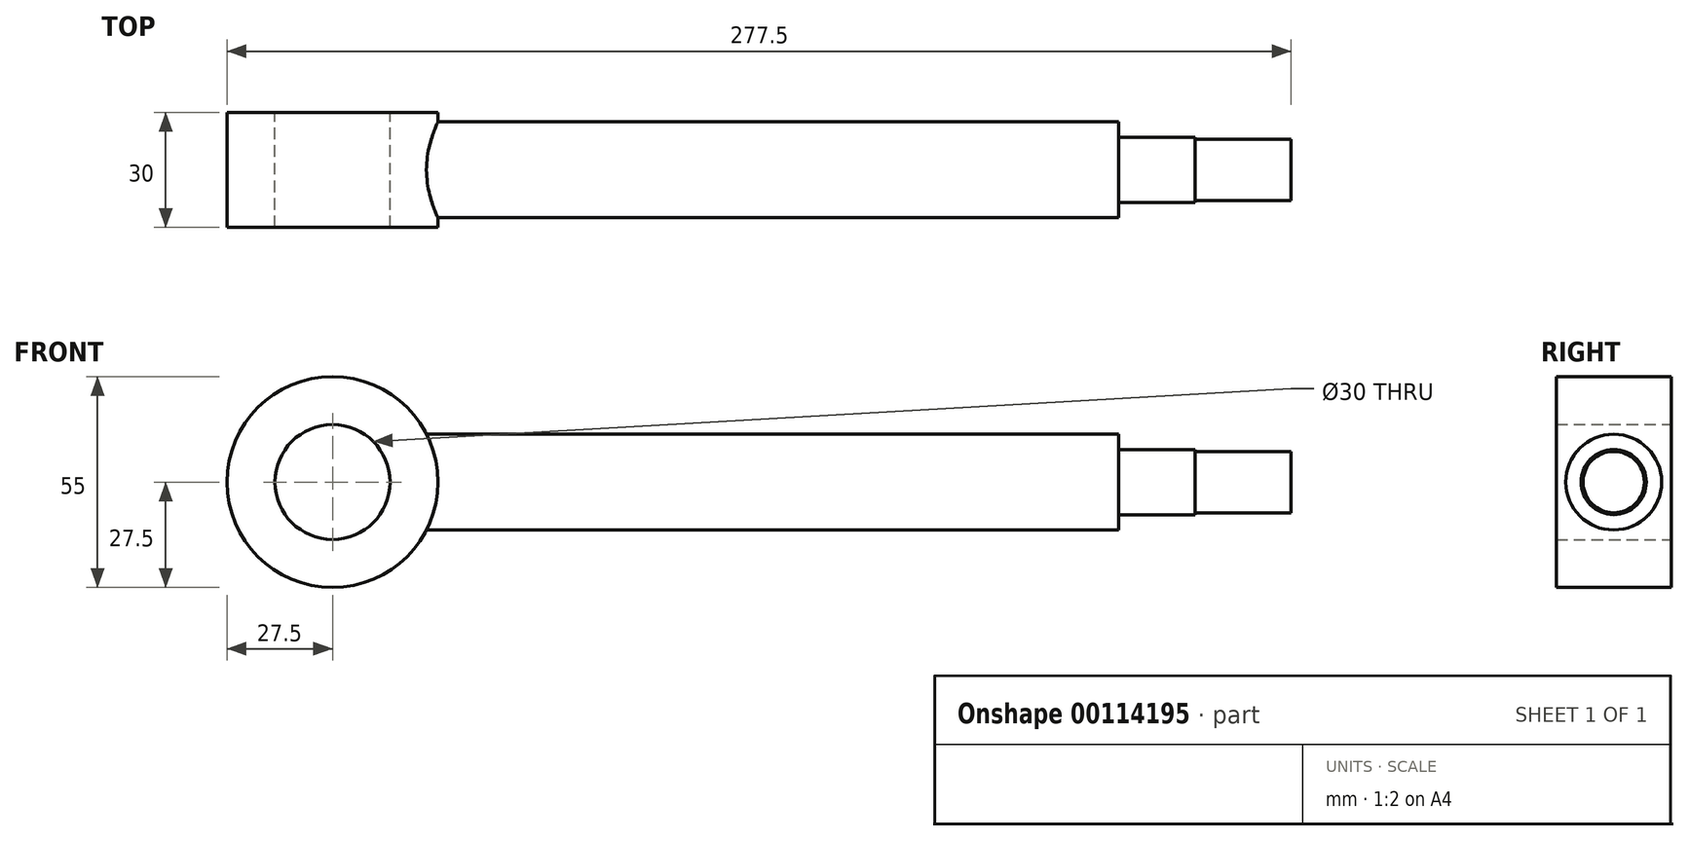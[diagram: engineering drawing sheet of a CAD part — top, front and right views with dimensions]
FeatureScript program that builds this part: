
annotation { "Feature Type Name" : "Feature", "Feature Type Description" : "" }
export const myFeature = defineFeature(function(context is Context, id is Id, definition is map)
    precondition{}
    {
        {
            var Q0;
            Q0=qCreatedBy(makeId("Front.planeOp"),FACE);
            var sketch = newSketch(context, id + "F0", { "sketchPlane" : qUnion([Q0])});
            skLineSegment(sketch, "E0", {"start": v(0, 0) * mm, "end": v(250.98, 0) * mm});
            skCircle(sketch, "E1", {"center": v(0, 0) * mm, "radius": 15 * mm});
            skCircle(sketch, "E2", {"center": v(0, 0) * mm, "radius": 27.5 * mm});
            skLineSegment(sketch, "E3", {"start": v(24.5, 12.5) * mm, "end": v(205, 12.5) * mm});
            skLineSegment(sketch, "E4", {"start": v(250, 8) * mm, "end": v(250, 0) * mm});
            skLineSegment(sketch, "E5", {"start": v(205, 12.5) * mm, "end": v(205, 8.5) * mm});
            skLineSegment(sketch, "E6", {"start": v(205, 8.5) * mm, "end": v(225, 8.5) * mm});
            skLineSegment(sketch, "E7", {"start": v(225, 8.5) * mm, "end": v(225, 8) * mm});
            skLineSegment(sketch, "E8", {"start": v(225, 8) * mm, "end": v(250, 8) * mm});
            skSolve(sketch);
        }
        {
            var Q0;
            Q0=qCreatedBy(makeId("Front.planeOp"),FACE);
            var sketch = newSketch(context, id + "F1", { "sketchPlane" : qUnion([Q0])});
            skLineSegment(sketch, "E9", {"start": v(54.7, 12.5) * mm, "end": v(54.7, 29) * mm});
            skLineSegment(sketch, "E10", {"start": v(54.7, 29) * mm, "end": v(60.7, 29) * mm});
            skLineSegment(sketch, "E11", {"start": v(60.7, 29) * mm, "end": v(60.7, 27.5) * mm});
            skLineSegment(sketch, "E12", {"start": v(60.7, 27.5) * mm, "end": v(76.24, 27.5) * mm});
            skLineSegment(sketch, "E13", {"start": v(76.24, 27.5) * mm, "end": v(79.7, 25.5) * mm});
            skLineSegment(sketch, "E14", {"start": v(79.7, 25.5) * mm, "end": v(94.7, 25.5) * mm});
            skLineSegment(sketch, "E15", {"start": v(94.7, 25.5) * mm, "end": v(94.7, 12.5) * mm});
            skLineSegment(sketch, "E16", {"start": v(94.7, 12.5) * mm, "end": v(54.7, 12.5) * mm});
            skLineSegment(sketch, "E17", {"start": v(66.7, 12.5) * mm, "end": v(66.7, 18) * mm});
            skLineSegment(sketch, "E18", {"start": v(66.7, 18) * mm, "end": v(76.7, 18) * mm});
            skLineSegment(sketch, "E19", {"start": v(76.7, 18) * mm, "end": v(76.7, 12.5) * mm});
            skLineSegment(sketch, "E20", {"start": v(54.7, 14) * mm, "end": v(56.7, 14) * mm});
            skLineSegment(sketch, "E21", {"start": v(56.7, 14) * mm, "end": v(56.7, 16) * mm});
            skLineSegment(sketch, "E22", {"start": v(56.7, 16) * mm, "end": v(60.7, 16) * mm});
            skLineSegment(sketch, "E23", {"start": v(60.7, 16) * mm, "end": v(60.7, 12.5) * mm});
            skLineSegment(sketch, "E24.bottom", {"start": v(85.7, 25.5) * mm, "end": v(89.7, 25.5) * mm});
            skLineSegment(sketch, "E24.top", {"start": v(85.7, 23.5) * mm, "end": v(89.7, 23.5) * mm});
            skLineSegment(sketch, "E24.left", {"start": v(85.7, 25.5) * mm, "end": v(85.7, 23.5) * mm});
            skLineSegment(sketch, "E24.right", {"start": v(89.7, 25.5) * mm, "end": v(89.7, 23.5) * mm});
            skLineSegment(sketch, "E25", {"start": v(48.25, 0) * mm, "end": v(103.65, 0) * mm});
            skSolve(sketch);
        }
        {
            var Q0;
            {var subQ1=sQuery(id+"F0.wireOp",EDGE,"E3");Q0=makeQuery(id+"F0.imprint","IMPRINT",FACE,{"disambiguationData":[TD([[makeQuery(id+"F0.imprint","IMPRINT",EDGE,{"derivedFrom":subQ1}),-1.0]])]});}
            var Q1;
            Q1=sQuery(id+"F0.wireOp",EDGE,"E0");
            revolve(context, id + "F2", {"entities" : qUnion([Q0]), "axis" : qUnion([Q1]), "revolveType" : RevolveType.FULL});
        }
        {
            var Q0;
            Q0=makeQuery(id+"F0.imprint","IMPRINT",FACE,{"disambiguationData":[TD([[makeQuery(id+"F0.imprint","IMPRINT",EDGE,{"derivedFrom":sQuery(id+"F0.wireOp",EDGE,"E1")}),-1.0]])]});
            extrude(context, id + "F3", {"entities" : qUnion([Q0]), "operationType" : NewBodyOperationType.ADD, "endBound" : BoundingType.SYMMETRIC, "depth" : 30 * mm});
        }
    });
